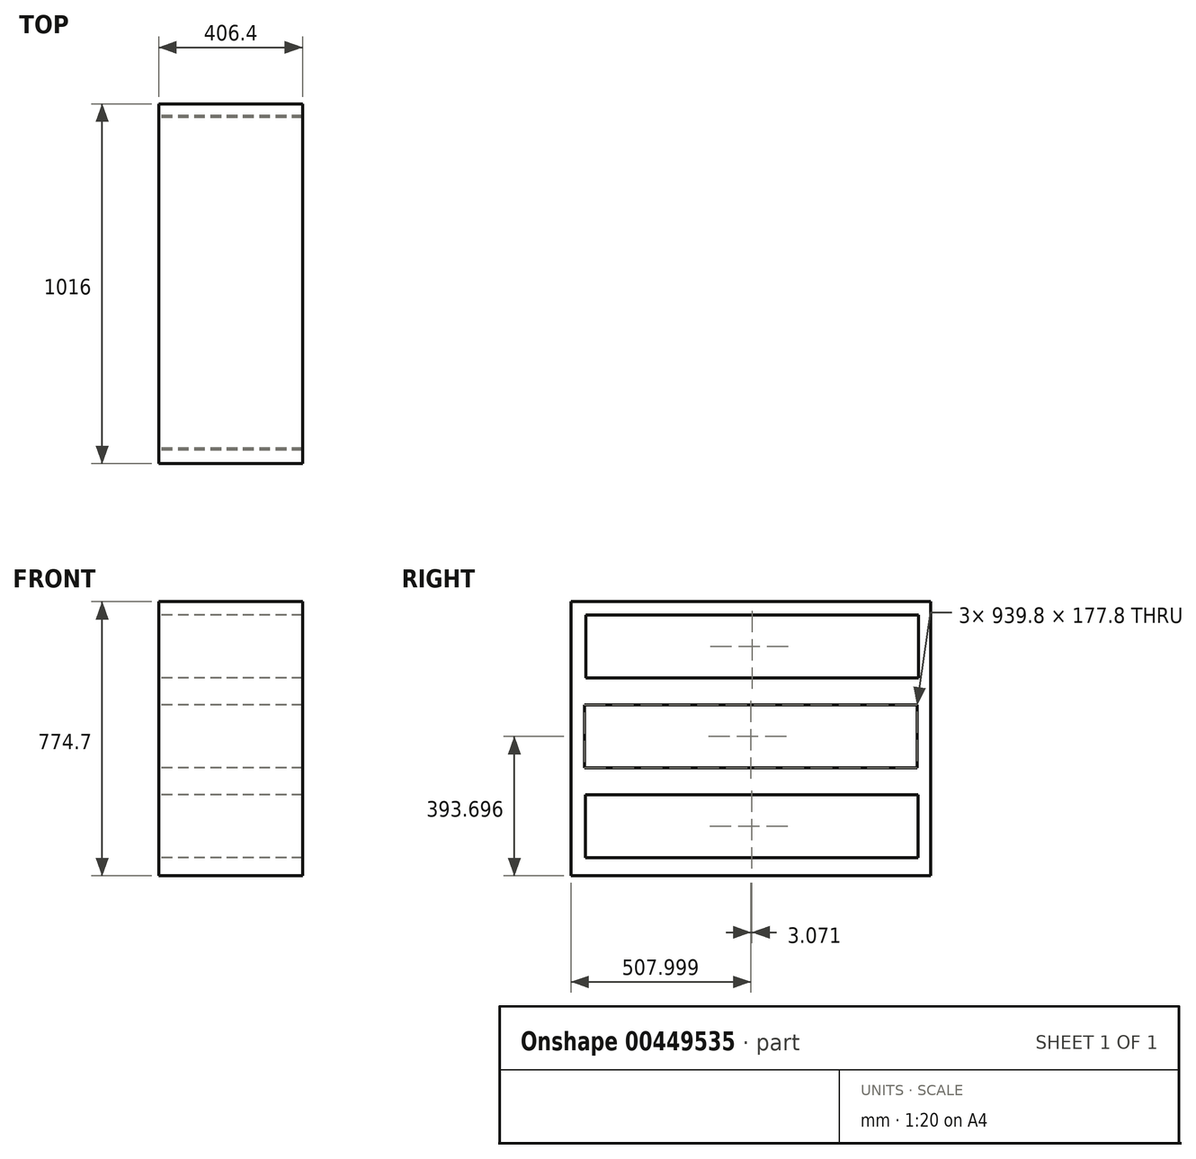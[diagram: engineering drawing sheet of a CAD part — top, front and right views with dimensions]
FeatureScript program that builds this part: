
annotation { "Feature Type Name" : "Feature", "Feature Type Description" : "" }
export const myFeature = defineFeature(function(context is Context, id is Id, definition is map)
    precondition{}
    {
        {
            var Q0;
            Q0=qCreatedBy(makeId("Right.planeOp"),FACE);
            var sketch = newSketch(context, id + "F0", { "sketchPlane" : qUnion([Q0])});
            skLineSegment(sketch, "E0.bottom", {"start": v(2075.48, -742.7) * mm, "end": v(3294.68, -742.7) * mm});
            skLineSegment(sketch, "E1.bottom", {"start": v(3294.68, 32) * mm, "end": v(4310.68, 32) * mm});
            skLineSegment(sketch, "E1.top", {"start": v(3294.68, -742.7) * mm, "end": v(4310.68, -742.7) * mm});
            skLineSegment(sketch, "E1.left", {"start": v(3294.68, 32) * mm, "end": v(3294.68, -742.7) * mm});
            skLineSegment(sketch, "E1.right", {"start": v(4310.68, 32) * mm, "end": v(4310.68, -742.7) * mm});
            skLineSegment(sketch, "E2.bottom", {"start": v(342.18, 139.96) * mm, "end": v(1561.38, 139.96) * mm});
            skLineSegment(sketch, "E2.top", {"start": v(342.18, -742.7) * mm, "end": v(1561.38, -742.7) * mm});
            skLineSegment(sketch, "E2.left", {"start": v(342.18, 139.96) * mm, "end": v(342.18, -742.7) * mm});
            skLineSegment(sketch, "E2.right", {"start": v(1561.38, 139.96) * mm, "end": v(1561.38, -742.7) * mm});
            skLineSegment(sketch, "E3.bottom", {"start": v(392.98, -742.7) * mm, "end": v(1459.78, -742.7) * mm});
            skLineSegment(sketch, "E3.top", {"start": v(392.98, -463.3) * mm, "end": v(1459.78, -463.3) * mm});
            skLineSegment(sketch, "E3.left", {"start": v(392.98, -742.7) * mm, "end": v(392.98, -463.3) * mm});
            skLineSegment(sketch, "E3.right", {"start": v(1459.78, -742.7) * mm, "end": v(1459.78, -463.3) * mm});
            skLineSegment(sketch, "E4.bottom", {"start": v(281.2, 12.96) * mm, "end": v(1297.2, 12.96) * mm});
            skLineSegment(sketch, "E4.top", {"start": v(281.2, -126.74) * mm, "end": v(1297.2, -126.74) * mm});
            skLineSegment(sketch, "E4.left", {"start": v(281.2, 12.96) * mm, "end": v(281.2, -126.74) * mm});
            skLineSegment(sketch, "E4.right", {"start": v(1297.2, 12.96) * mm, "end": v(1297.2, -126.74) * mm});
            skLineSegment(sketch, "E5.bottom", {"start": v(-719.9, -635.87) * mm, "end": v(42, -635.87) * mm});
            skLineSegment(sketch, "E5.top", {"start": v(-719.9, -742.7) * mm, "end": v(42, -742.7) * mm});
            skLineSegment(sketch, "E5.left", {"start": v(42, -635.87) * mm, "end": v(42, -742.7) * mm});
            skLineSegment(sketch, "E5.right", {"start": v(-719.9, -635.87) * mm, "end": v(-719.9, -742.7) * mm});
            skLineSegment(sketch, "E6", {"start": v(42, -742.7) * mm, "end": v(3294.68, -742.7) * mm});
            skLineSegment(sketch, "E7", {"start": v(-719.9, -742.7) * mm, "end": v(4310.68, -742.7) * mm});
            skLineSegment(sketch, "E8.bottom", {"start": v(-800.03, 32) * mm, "end": v(215.97, 32) * mm});
            skLineSegment(sketch, "E9.top", {"start": v(342.18, 1054.36) * mm, "end": v(1561.38, 1054.36) * mm});
            skLineSegment(sketch, "E9.left", {"start": v(342.18, 139.96) * mm, "end": v(342.18, 1054.36) * mm});
            skLineSegment(sketch, "E9.right", {"start": v(1561.38, 139.96) * mm, "end": v(1561.38, 1054.36) * mm});
            skLineSegment(sketch, "E10.bottom", {"start": v(380.28, 139.96) * mm, "end": v(1523.28, 139.96) * mm});
            skLineSegment(sketch, "E10.top", {"start": v(380.28, 411.17) * mm, "end": v(1523.28, 411.17) * mm});
            skLineSegment(sketch, "E10.left", {"start": v(380.28, 139.96) * mm, "end": v(380.28, 411.17) * mm});
            skLineSegment(sketch, "E10.right", {"start": v(1523.28, 139.96) * mm, "end": v(1523.28, 411.17) * mm});
            skLineSegment(sketch, "E11", {"start": v(342.18, 108.2) * mm, "end": v(1561.38, 108.2) * mm});
            skLineSegment(sketch, "E12.bottom", {"start": v(443.78, -374.4) * mm, "end": v(1459.78, -374.4) * mm});
            skLineSegment(sketch, "E12.top", {"start": v(443.78, -139.44) * mm, "end": v(1459.78, -139.44) * mm});
            skLineSegment(sketch, "E12.left", {"start": v(443.78, -374.4) * mm, "end": v(443.78, -139.44) * mm});
            skLineSegment(sketch, "E12.right", {"start": v(1459.78, -374.4) * mm, "end": v(1459.78, -139.44) * mm});
            skLineSegment(sketch, "E13.bottom", {"start": v(1523.28, 139.96) * mm, "end": v(380.28, 139.96) * mm});
            skLineSegment(sketch, "E13.top", {"start": v(1523.28, 178.06) * mm, "end": v(380.28, 178.06) * mm});
            skLineSegment(sketch, "E13.left", {"start": v(1523.28, 139.96) * mm, "end": v(1523.28, 178.06) * mm});
            skLineSegment(sketch, "E13.right", {"start": v(380.28, 139.96) * mm, "end": v(380.28, 178.06) * mm});
            skLineSegment(sketch, "E14.bottom", {"start": v(4250.99, -701.36) * mm, "end": v(3355.11, -701.36) * mm});
            skLineSegment(sketch, "E14.top", {"start": v(4250.99, -14) * mm, "end": v(3355.11, -14) * mm});
            skLineSegment(sketch, "E14.left", {"start": v(4250.99, -701.36) * mm, "end": v(4250.99, -14) * mm});
            skLineSegment(sketch, "E14.right", {"start": v(3355.11, -701.36) * mm, "end": v(3355.11, -14) * mm});
            skPoint(sketch, "E14.middle", {"position": v(3803.05, -357.68) * mm});
            skSolve(sketch);
        }
        {
            var Q0;
            Q0=makeQuery(id+"F0.imprint","IMPRINT",FACE,{"disambiguationData":[TD([[makeQuery(id+"F0.imprint","IMPRINT",EDGE,{"derivedFrom":sQuery(id+"F0.wireOp",EDGE,"E14.bottom")}),-1.0]])]});
            var sketch = newSketch(context, id + "F1", { "sketchPlane" : qUnion([Q0])});
            skLineSegment(sketch, "E15.bottom", {"start": v(1882.83, 32) * mm, "end": v(2898.83, 32) * mm});
            skLineSegment(sketch, "E15.top", {"start": v(1882.83, -742.7) * mm, "end": v(2898.83, -742.7) * mm});
            skLineSegment(sketch, "E15.left", {"start": v(1882.83, 32) * mm, "end": v(1882.83, -742.7) * mm});
            skLineSegment(sketch, "E15.right", {"start": v(2898.83, 32) * mm, "end": v(2898.83, -742.7) * mm});
            skLineSegment(sketch, "E16.bottom", {"start": v(2860.73, -437.9) * mm, "end": v(1920.93, -437.9) * mm});
            skLineSegment(sketch, "E16.top", {"start": v(2860.73, -260.1) * mm, "end": v(1920.93, -260.1) * mm});
            skLineSegment(sketch, "E16.left", {"start": v(2860.73, -437.9) * mm, "end": v(2860.73, -260.1) * mm});
            skLineSegment(sketch, "E16.right", {"start": v(1920.93, -437.9) * mm, "end": v(1920.93, -260.1) * mm});
            skLineSegment(sketch, "E17.bottom", {"start": v(2865.3, -183.9) * mm, "end": v(1925.5, -183.9) * mm});
            skLineSegment(sketch, "E17.top", {"start": v(2865.3, -6.1) * mm, "end": v(1925.5, -6.1) * mm});
            skLineSegment(sketch, "E17.left", {"start": v(2865.3, -183.9) * mm, "end": v(2865.3, -6.1) * mm});
            skLineSegment(sketch, "E17.right", {"start": v(1925.5, -183.9) * mm, "end": v(1925.5, -6.1) * mm});
            skLineSegment(sketch, "E18.bottom", {"start": v(2863.8, -691.9) * mm, "end": v(1924, -691.9) * mm});
            skLineSegment(sketch, "E18.top", {"start": v(2863.8, -514.1) * mm, "end": v(1924, -514.1) * mm});
            skLineSegment(sketch, "E18.left", {"start": v(2863.8, -691.9) * mm, "end": v(2863.8, -514.1) * mm});
            skLineSegment(sketch, "E18.right", {"start": v(1924, -691.9) * mm, "end": v(1924, -514.1) * mm});
            skSolve(sketch);
        }
        {
            var Q0;
            Q0=makeQuery(id+"F1.imprint","IMPRINT",FACE,{"disambiguationData":[TD([[makeQuery(id+"F1.imprint","IMPRINT",EDGE,{"derivedFrom":sQuery(id+"F1.wireOp",EDGE,"E15.bottom")}),-1.0]])]});
            extrude(context, id + "F2", {"entities" : qUnion([Q0]), "depth" : 406.4 * mm, "offsetDistance" : 25.4 * mm});
        }
    });
